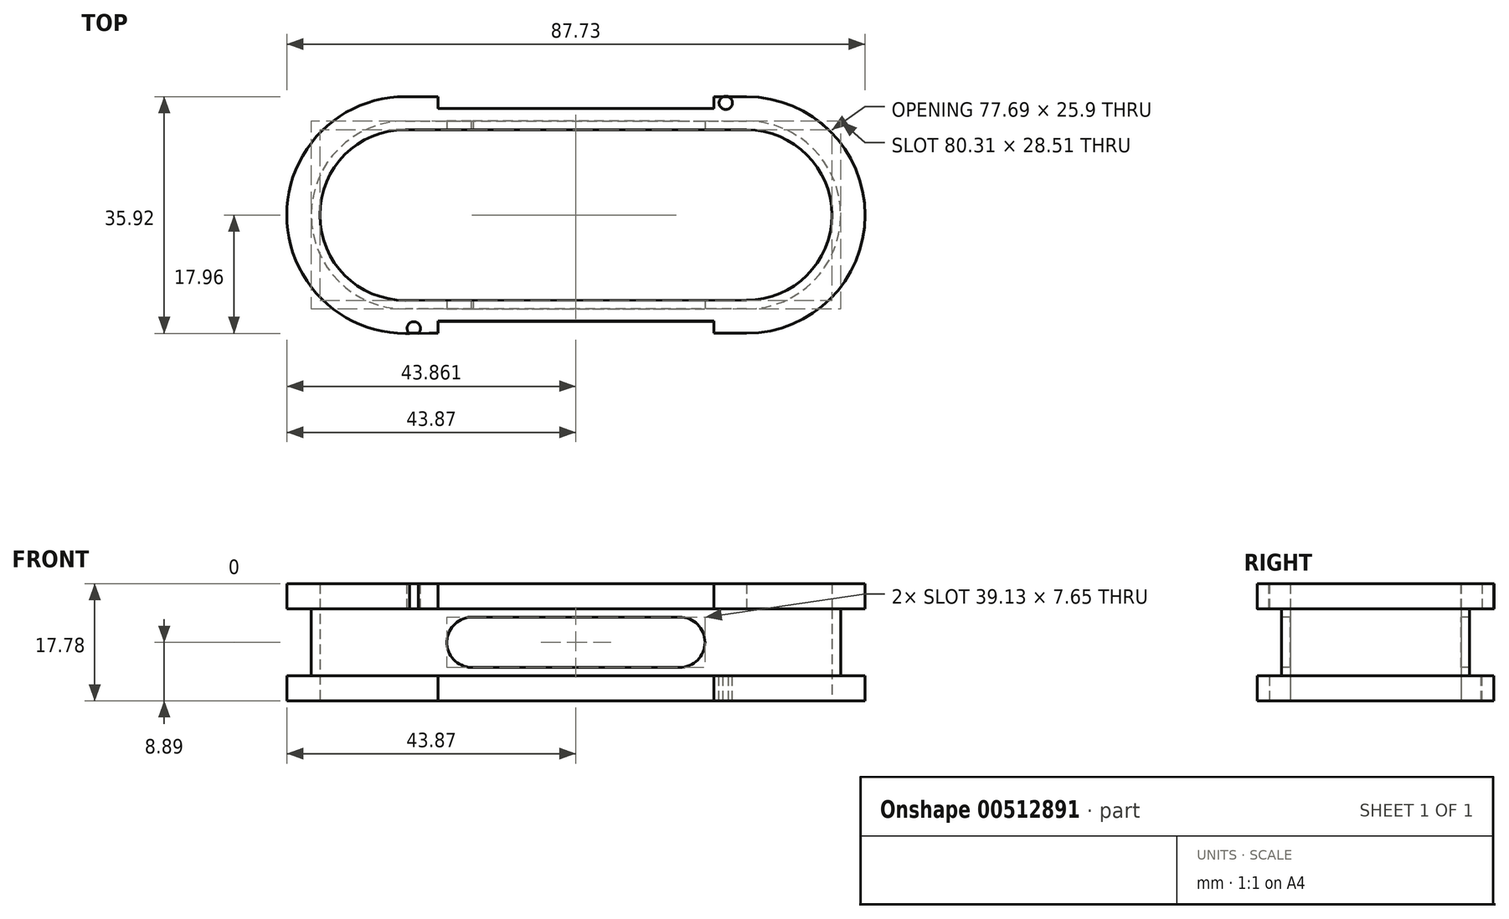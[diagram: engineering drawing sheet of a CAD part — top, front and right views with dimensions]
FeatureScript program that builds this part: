
annotation { "Feature Type Name" : "Feature", "Feature Type Description" : "" }
export const myFeature = defineFeature(function(context is Context, id is Id, definition is map)
    precondition{}
    {
        {
            var Q0;
            Q0=qCreatedBy(makeId("Top.planeOp"),FACE);
            var sketch = newSketch(context, id + "F0", { "sketchPlane" : qUnion([Q0])});
            skLineSegment(sketch, "E0.left", {"start": v(0, 0) * mm, "end": v(0, 0) * mm});
            skLineSegment(sketch, "E0.right", {"start": v(25.9, 0) * mm, "end": v(25.9, 0) * mm});
            skLineSegment(sketch, "E1.top", {"start": v(0, 12.95) * mm, "end": v(0, 12.95) * mm});
            skLineSegment(sketch, "E2.top", {"start": v(25.9, 12.95) * mm, "end": v(25.9, 12.95) * mm});
            skLineSegment(sketch, "E3.bottom", {"start": v(25.9, 12.95) * mm, "end": v(-25.9, 12.95) * mm});
            skLineSegment(sketch, "E3.top", {"start": v(25.9, -12.95) * mm, "end": v(-25.9, -12.95) * mm});
            skPoint(sketch, "E3.middle", {"position": v(0, 0) * mm});
            skArc(sketch, "E4", {"start": v(-25.9, 12.95) * mm, "mid": v(-38.85, 0) * mm, "end": v(-25.9, -12.95) * mm});
            skArc(sketch, "E5", {"start": v(25.9, -12.95) * mm, "mid": v(38.85, 0) * mm, "end": v(25.9, 12.95) * mm});
            skLineSegment(sketch, "E6", {"start": v(20.9, 17.95) * mm, "end": v(25.9, 17.95) * mm});
            skLineSegment(sketch, "E7", {"start": v(-20.9, 17.95) * mm, "end": v(-25.9, 17.95) * mm});
            skArc(sketch, "E8", {"start": v(-25.9, 17.95) * mm, "mid": v(-43.86, 0) * mm, "end": v(-25.9, -17.95) * mm});
            skArc(sketch, "E9.trimOffspring", {"start": v(25.9, -17.95) * mm, "mid": v(43.86, 0) * mm, "end": v(25.9, 17.95) * mm});
            skLineSegment(sketch, "E10", {"start": v(-20.9, 16.1) * mm, "end": v(-20.9, 17.95) * mm});
            skLineSegment(sketch, "E11", {"start": v(-25.9, -17.95) * mm, "end": v(-20.9, -17.95) * mm});
            skLineSegment(sketch, "E12", {"start": v(-20.9, -12.95) * mm, "end": v(-20.9, -17.95) * mm});
            skLineSegment(sketch, "E13", {"start": v(20.9, -12.95) * mm, "end": v(20.9, -17.95) * mm});
            skPoint(sketch, "E13.startSnap0", {"position": v(0, -12.95) * mm});
            skPoint(sketch, "E13.endSnap0", {"position": v(0, -17.95) * mm});
            skLineSegment(sketch, "E14", {"start": v(20.9, 16.1) * mm, "end": v(20.9, 17.95) * mm});
            skLineSegment(sketch, "E15.trimOffspring", {"start": v(20.9, -17.95) * mm, "end": v(25.9, -17.95) * mm});
            skLineSegment(sketch, "E16", {"start": v(-20.9, -16.13) * mm, "end": v(20.9, -16.13) * mm});
            skPoint(sketch, "E17.orphan", {"position": v(-25.9, -16.13) * mm});
            skLineSegment(sketch, "E18.trimOffspring", {"start": v(-20.9, 16.1) * mm, "end": v(20.9, 16.1) * mm});
            skSolve(sketch);
        }
        {
            var Q0;
            Q0 = qSketchRegion(id + "F0", true);
            extrude(context, id + "F1", {"entities" : qUnion([Q0]), "depth" : 3.8 * mm});
        }
        {
            var Q0;
            Q0=makeQuery(id+"F1.opExtrude","CAP_FACE",FACE,{"disambiguationData":[OSD([sQuery(id+"F0.wireOp",EDGE,"E3.bottom"),sQuery(id+"F0.wireOp",EDGE,"E3.top"),sQuery(id+"F0.wireOp",EDGE,"E4"),sQuery(id+"F0.wireOp",EDGE,"E5"),sQuery(id+"F0.wireOp",EDGE,"E6"),sQuery(id+"F0.wireOp",EDGE,"E7"),sQuery(id+"F0.wireOp",EDGE,"E8"),sQuery(id+"F0.wireOp",EDGE,"E9.trimOffspring"),sQuery(id+"F0.wireOp",EDGE,"E10"),sQuery(id+"F0.wireOp",EDGE,"E11"),sQuery(id+"F0.wireOp",EDGE,"E12"),sQuery(id+"F0.wireOp",EDGE,"E13"),sQuery(id+"F0.wireOp",EDGE,"E14"),sQuery(id+"F0.wireOp",EDGE,"E15.trimOffspring"),sQuery(id+"F0.wireOp",EDGE,"E16"),sQuery(id+"F0.wireOp",EDGE,"E18.trimOffspring")])],"isStart":false});
            var sketch = newSketch(context, id + "F2", { "sketchPlane" : qUnion([Q0])});
            skLineSegment(sketch, "E19", {"start": v(20.9, 17.03) * mm, "end": v(32.8, 17.03) * mm});
            skLineSegment(sketch, "E20", {"start": v(22.73, 17.03) * mm, "end": v(22.73, 17.95) * mm});
            skCircle(sketch, "E21", {"center": v(22.73, 17.03) * mm, "radius": 1.02 * mm});
            skSolve(sketch);
        }
        {
            var Q0;
            Q0=sQuery(id+"F2.wireOp",VERTEX,"E21.center");
            var Q1;
            Q1=makeQuery(id+"F1.opExtrude","SWEPT_BODY",BODY,{"disambiguationData":[OSD([sQuery(id+"F0.wireOp",EDGE,"E3.bottom"),sQuery(id+"F0.wireOp",EDGE,"E3.top"),sQuery(id+"F0.wireOp",EDGE,"E4"),sQuery(id+"F0.wireOp",EDGE,"E5"),sQuery(id+"F0.wireOp",EDGE,"E6"),sQuery(id+"F0.wireOp",EDGE,"E7"),sQuery(id+"F0.wireOp",EDGE,"E8"),sQuery(id+"F0.wireOp",EDGE,"E9.trimOffspring"),sQuery(id+"F0.wireOp",EDGE,"E10"),sQuery(id+"F0.wireOp",EDGE,"E11"),sQuery(id+"F0.wireOp",EDGE,"E12"),sQuery(id+"F0.wireOp",EDGE,"E13"),sQuery(id+"F0.wireOp",EDGE,"E14"),sQuery(id+"F0.wireOp",EDGE,"E15.trimOffspring"),sQuery(id+"F0.wireOp",EDGE,"E16"),sQuery(id+"F0.wireOp",EDGE,"E18.trimOffspring")])]});
            hole(context, id + "F3", {"style" : HoleStyle.SIMPLE, "endStyle" : HoleEndStyle.BLIND, "holeDiameter" : 2.03 * mm, "holeDepth" : 12.7 * mm, "isTappedThrough" : true, "tappedDepth" : 12.7 * mm, "tapClearance" : 3, "locations" : qUnion([Q0]), "scope" : qUnion([Q1])});
        }
        {
            var Q0;
            Q0=makeQuery(id+"F1.opExtrude","CAP_FACE",FACE,{"disambiguationData":[OSD([sQuery(id+"F0.wireOp",EDGE,"E3.bottom"),sQuery(id+"F0.wireOp",EDGE,"E3.top"),sQuery(id+"F0.wireOp",EDGE,"E4"),sQuery(id+"F0.wireOp",EDGE,"E5"),sQuery(id+"F0.wireOp",EDGE,"E6"),sQuery(id+"F0.wireOp",EDGE,"E7"),sQuery(id+"F0.wireOp",EDGE,"E8"),sQuery(id+"F0.wireOp",EDGE,"E9.trimOffspring"),sQuery(id+"F0.wireOp",EDGE,"E10"),sQuery(id+"F0.wireOp",EDGE,"E11"),sQuery(id+"F0.wireOp",EDGE,"E12"),sQuery(id+"F0.wireOp",EDGE,"E13"),sQuery(id+"F0.wireOp",EDGE,"E14"),sQuery(id+"F0.wireOp",EDGE,"E15.trimOffspring"),sQuery(id+"F0.wireOp",EDGE,"E16"),sQuery(id+"F0.wireOp",EDGE,"E18.trimOffspring")])],"isStart":false});
            var sketch = newSketch(context, id + "F4", { "sketchPlane" : qUnion([Q0])});
            skLineSegment(sketch, "E22", {"start": v(-20.9, 14.25) * mm, "end": v(-25.9, 14.25) * mm});
            skArc(sketch, "E23", {"start": v(-25.9, 14.25) * mm, "mid": v(-40.16, 0) * mm, "end": v(-25.9, -14.25) * mm});
            skLineSegment(sketch, "E24", {"start": v(-20.9, -14.25) * mm, "end": v(-25.9, -14.25) * mm});
            skPoint(sketch, "E25.center.orphan", {"position": v(-20.9, 0) * mm});
            skLineSegment(sketch, "E26", {"start": v(-20.9, 14.25) * mm, "end": v(25.9, 14.25) * mm});
            skLineSegment(sketch, "E27", {"start": v(-25.9, -14.25) * mm, "end": v(25.9, -14.25) * mm});
            skArc(sketch, "E28", {"start": v(25.9, -14.25) * mm, "mid": v(40.16, 0) * mm, "end": v(25.9, 14.25) * mm});
            skPoint(sketch, "E29.orphan", {"position": v(-20.9, 17.95) * mm});
            skPoint(sketch, "E30.trimOffspring.end.orphan", {"position": v(-20.9, -17.95) * mm});
            skArc(sketch, "E31", {"start": v(-25.9, 12.95) * mm, "mid": v(-38.85, 0) * mm, "end": v(-25.9, -12.95) * mm});
            skArc(sketch, "E32", {"start": v(25.9, -12.95) * mm, "mid": v(38.85, 0) * mm, "end": v(25.9, 12.95) * mm});
            skLineSegment(sketch, "E33", {"start": v(-25.9, 12.95) * mm, "end": v(25.9, 12.95) * mm});
            skLineSegment(sketch, "E34", {"start": v(25.9, -12.95) * mm, "end": v(-25.9, -12.95) * mm});
            skSolve(sketch);
        }
        {
            var Q0;
            Q0 = qSketchRegion(id + "F4", true);
            extrude(context, id + "F5", {"entities" : qUnion([Q0]), "operationType" : NewBodyOperationType.ADD, "depth" : 10.16 * mm});
        }
        {
            var Q0;
            Q0=makeQuery(id+"F5.opExtrude","CAP_FACE",FACE,{"disambiguationData":[OSD([sQuery(id+"F4.wireOp",EDGE,"E22"),sQuery(id+"F4.wireOp",EDGE,"E23"),sQuery(id+"F4.wireOp",EDGE,"E26"),sQuery(id+"F4.wireOp",EDGE,"E27"),sQuery(id+"F4.wireOp",EDGE,"E28"),sQuery(id+"F4.wireOp",EDGE,"E31"),sQuery(id+"F4.wireOp",EDGE,"E32"),sQuery(id+"F4.wireOp",EDGE,"E33"),sQuery(id+"F4.wireOp",EDGE,"E34")])],"isStart":false});
            var sketch = newSketch(context, id + "F6", { "sketchPlane" : qUnion([Q0])});
            skLineSegment(sketch, "E35", {"start": v(-20.9, 17.95) * mm, "end": v(-20.9, 16.18) * mm});
            skLineSegment(sketch, "E36", {"start": v(25.9, 12.95) * mm, "end": v(25.9, 12.93) * mm});
            skPoint(sketch, "E37", {"position": v(-43.87, 0) * mm});
            skArc(sketch, "E38", {"start": v(-25.86, 17.96) * mm, "mid": v(-43.87, 0) * mm, "end": v(-25.86, -17.96) * mm});
            skPoint(sketch, "E39", {"position": v(43.86, 0) * mm});
            skArc(sketch, "E40", {"start": v(25.9, -17.95) * mm, "mid": v(43.86, 0) * mm, "end": v(25.9, 17.95) * mm});
            skArc(sketch, "E41", {"start": v(25.9, -12.93) * mm, "mid": v(38.84, 0) * mm, "end": v(25.9, 12.93) * mm});
            skArc(sketch, "E42", {"start": v(-25.9, 12.95) * mm, "mid": v(-38.85, 0) * mm, "end": v(-25.9, -12.95) * mm});
            skLineSegment(sketch, "E43", {"start": v(-20.9, 17.95) * mm, "end": v(-25.86, 17.96) * mm});
            skLineSegment(sketch, "E44", {"start": v(-20.9, -17.95) * mm, "end": v(-25.86, -17.96) * mm});
            skLineSegment(sketch, "E45", {"start": v(20.9, 17.96) * mm, "end": v(20.9, 16.18) * mm});
            skLineSegment(sketch, "E46", {"start": v(20.9, 17.96) * mm, "end": v(25.9, 17.95) * mm});
            skLineSegment(sketch, "E47", {"start": v(20.9, -17.96) * mm, "end": v(25.9, -17.95) * mm});
            skLineSegment(sketch, "E48.trimOffspring", {"start": v(20.9, -16.1) * mm, "end": v(20.9, -17.96) * mm});
            skLineSegment(sketch, "E49.trimOffspring", {"start": v(25.9, -12.93) * mm, "end": v(25.9, -12.95) * mm});
            skLineSegment(sketch, "E50", {"start": v(-25.9, 12.95) * mm, "end": v(25.9, 12.95) * mm});
            skLineSegment(sketch, "E51", {"start": v(-25.9, -12.95) * mm, "end": v(25.9, -12.93) * mm});
            skLineSegment(sketch, "E52", {"start": v(-20.9, 16.18) * mm, "end": v(20.9, 16.18) * mm});
            skLineSegment(sketch, "E53", {"start": v(-20.9, -16.1) * mm, "end": v(20.9, -16.1) * mm});
            skLineSegment(sketch, "E54.trimOffspring", {"start": v(-20.9, -16.1) * mm, "end": v(-20.9, -17.95) * mm});
            skSolve(sketch);
        }
        {
            var Q0;
            Q0=makeQuery(id+"F6.imprint","IMPRINT",FACE,{"disambiguationData":[TD([[makeQuery(id+"F6.imprint","IMPRINT",EDGE,{"derivedFrom":sQuery(id+"F6.wireOp",EDGE,"E36")}),1.0]])]});
            var Q1;
            {var subQ0=sQuery(id+"F6.wireOp",EDGE,"E49.trimOffspring");Q1=makeQuery(id+"F6.imprint","IMPRINT",FACE,{"disambiguationData":[TD([[makeQuery(id+"F6.imprint","IMPRINT",EDGE,{"derivedFrom":subQ0}),-1.0]])]});}
            var Q2;
            {var subQ4=sQuery(id+"F6.wireOp",EDGE,"E50");Q2=makeQuery(id+"F6.imprint","IMPRINT",FACE,{"disambiguationData":[TD([[makeQuery(id+"F6.imprint","IMPRINT",EDGE,{"derivedFrom":subQ4}),-1.0]])]});}
            var Q3;
            Q3=makeQuery(id+"F6.imprint","IMPRINT",FACE,{"disambiguationData":[TD([[makeQuery(id+"F6.imprint","IMPRINT",EDGE,{"derivedFrom":sQuery(id+"F6.wireOp",EDGE,"E35")}),-1.0]])]});
            extrude(context, id + "F7", {"entities" : qUnion([Q0, Q1, Q2, Q3]), "operationType" : NewBodyOperationType.ADD, "depth" : 3.8 * mm});
        }
        {
            var Q0;
            Q0=makeQuery(id+"F7.opExtrude","CAP_FACE",FACE,{"disambiguationData":[OSD([sQuery(id+"F6.wireOp",EDGE,"E35"),sQuery(id+"F6.wireOp",EDGE,"E36"),sQuery(id+"F6.wireOp",EDGE,"E38"),sQuery(id+"F6.wireOp",EDGE,"E40"),sQuery(id+"F6.wireOp",EDGE,"E41"),sQuery(id+"F6.wireOp",EDGE,"E43"),sQuery(id+"F6.wireOp",EDGE,"E44"),sQuery(id+"F6.wireOp",EDGE,"E45"),sQuery(id+"F6.wireOp",EDGE,"E46"),sQuery(id+"F6.wireOp",EDGE,"E47"),sQuery(id+"F6.wireOp",EDGE,"E48.trimOffspring"),sQuery(id+"F6.wireOp",EDGE,"E50"),sQuery(id+"F6.wireOp",EDGE,"E51"),sQuery(id+"F6.wireOp",EDGE,"E52"),sQuery(id+"F6.wireOp",EDGE,"E53"),sQuery(id+"F6.wireOp",EDGE,"E54.trimOffspring"),sQuery(id+"F6.wireOp",EDGE,"E42")])],"isStart":false});
            var sketch = newSketch(context, id + "F8", { "sketchPlane" : qUnion([Q0])});
            skLineSegment(sketch, "E55", {"start": v(-20.9, -17.95) * mm, "end": v(-20.9, -12.95) * mm});
            skPoint(sketch, "E56.center.orphan", {"position": v(-22.75, -17.95) * mm});
            skArc(sketch, "E57", {"start": v(-24.6, -17.96) * mm, "mid": v(-24.6, -17.96) * mm, "end": v(-24.6, -17.96) * mm});
            skLineSegment(sketch, "E58", {"start": v(-24.6, -17.96) * mm, "end": v(-24.6, -16.43) * mm});
            skArc(sketch, "E59", {"start": v(-23.27, -17.2) * mm, "mid": v(-23.27, -17.2) * mm, "end": v(-23.27, -17.2) * mm});
            skLineSegment(sketch, "E60", {"start": v(-24.6, -17.2) * mm, "end": v(-23.27, -17.2) * mm});
            skSolve(sketch);
        }
        {
            var Q0;
            Q0=sQuery(id+"F8.wireOp",VERTEX,"E60.start");
            var Q1;
            Q1=makeQuery(id+"F1.opExtrude","SWEPT_BODY",BODY,{"disambiguationData":[OSD([sQuery(id+"F0.wireOp",EDGE,"E3.bottom"),sQuery(id+"F0.wireOp",EDGE,"E3.top"),sQuery(id+"F0.wireOp",EDGE,"E4"),sQuery(id+"F0.wireOp",EDGE,"E5"),sQuery(id+"F0.wireOp",EDGE,"E6"),sQuery(id+"F0.wireOp",EDGE,"E7"),sQuery(id+"F0.wireOp",EDGE,"E8"),sQuery(id+"F0.wireOp",EDGE,"E9.trimOffspring"),sQuery(id+"F0.wireOp",EDGE,"E10"),sQuery(id+"F0.wireOp",EDGE,"E11"),sQuery(id+"F0.wireOp",EDGE,"E12"),sQuery(id+"F0.wireOp",EDGE,"E13"),sQuery(id+"F0.wireOp",EDGE,"E14"),sQuery(id+"F0.wireOp",EDGE,"E15.trimOffspring"),sQuery(id+"F0.wireOp",EDGE,"E16"),sQuery(id+"F0.wireOp",EDGE,"E18.trimOffspring")])]});
            hole(context, id + "F9", {"style" : HoleStyle.SIMPLE, "endStyle" : HoleEndStyle.BLIND, "holeDiameter" : 2.03 * mm, "holeDepth" : 5.08 * mm, "isTappedThrough" : true, "tappedDepth" : 12.7 * mm, "tapClearance" : 3, "locations" : qUnion([Q0]), "scope" : qUnion([Q1])});
        }
        {
            var Q0;
            Q0=makeQuery(id+"F5.opExtrude","SWEPT_FACE",FACE,{"disambiguationData":[OSD([sQuery(id+"F4.wireOp",EDGE,"E27")])]});
            var sketch = newSketch(context, id + "F10", { "sketchPlane" : qUnion([Q0])});
            skPoint(sketch, "E61", {"position": v(0, 8.9) * mm});
            skPoint(sketch, "E62.orphan", {"position": v(-25.9, 13.97) * mm});
            skPoint(sketch, "E63.start.orphan", {"position": v(25.9, 3.81) * mm});
            skArc(sketch, "E64", {"start": v(-15.59, 12.71) * mm, "mid": v(-19.57, 8.89) * mm, "end": v(-15.59, 5.07) * mm});
            skLineSegment(sketch, "E65", {"start": v(-15.59, 12.71) * mm, "end": v(15.74, 12.71) * mm});
            skArc(sketch, "E66", {"start": v(15.74, 5.07) * mm, "mid": v(19.57, 8.9) * mm, "end": v(15.74, 12.71) * mm});
            skPoint(sketch, "E67.center.orphan", {"position": v(25.9, 8.9) * mm});
            skLineSegment(sketch, "E68", {"start": v(-15.9, 5.07) * mm, "end": v(15.74, 5.07) * mm});
            skPoint(sketch, "E69.center.orphan", {"position": v(-25.9, 8.89) * mm});
            skSolve(sketch);
        }
        {
            var Q0;
            {var subQ5=sQuery(id+"F10.wireOp",EDGE,"E65");Q0=makeQuery(id+"F10.imprint","IMPRINT",FACE,{"disambiguationData":[TD([[makeQuery(id+"F10.imprint","IMPRINT",EDGE,{"derivedFrom":subQ5}),-1.0]])]});}
            extrude(context, id + "F11", {"entities" : qUnion([Q0]), "operationType" : NewBodyOperationType.REMOVE, "endBound" : BoundingType.THROUGH_ALL, "oppositeDirection" : true, "depth" : 25.4 * mm, "offsetDistance" : 25.4 * mm});
        }
    });
